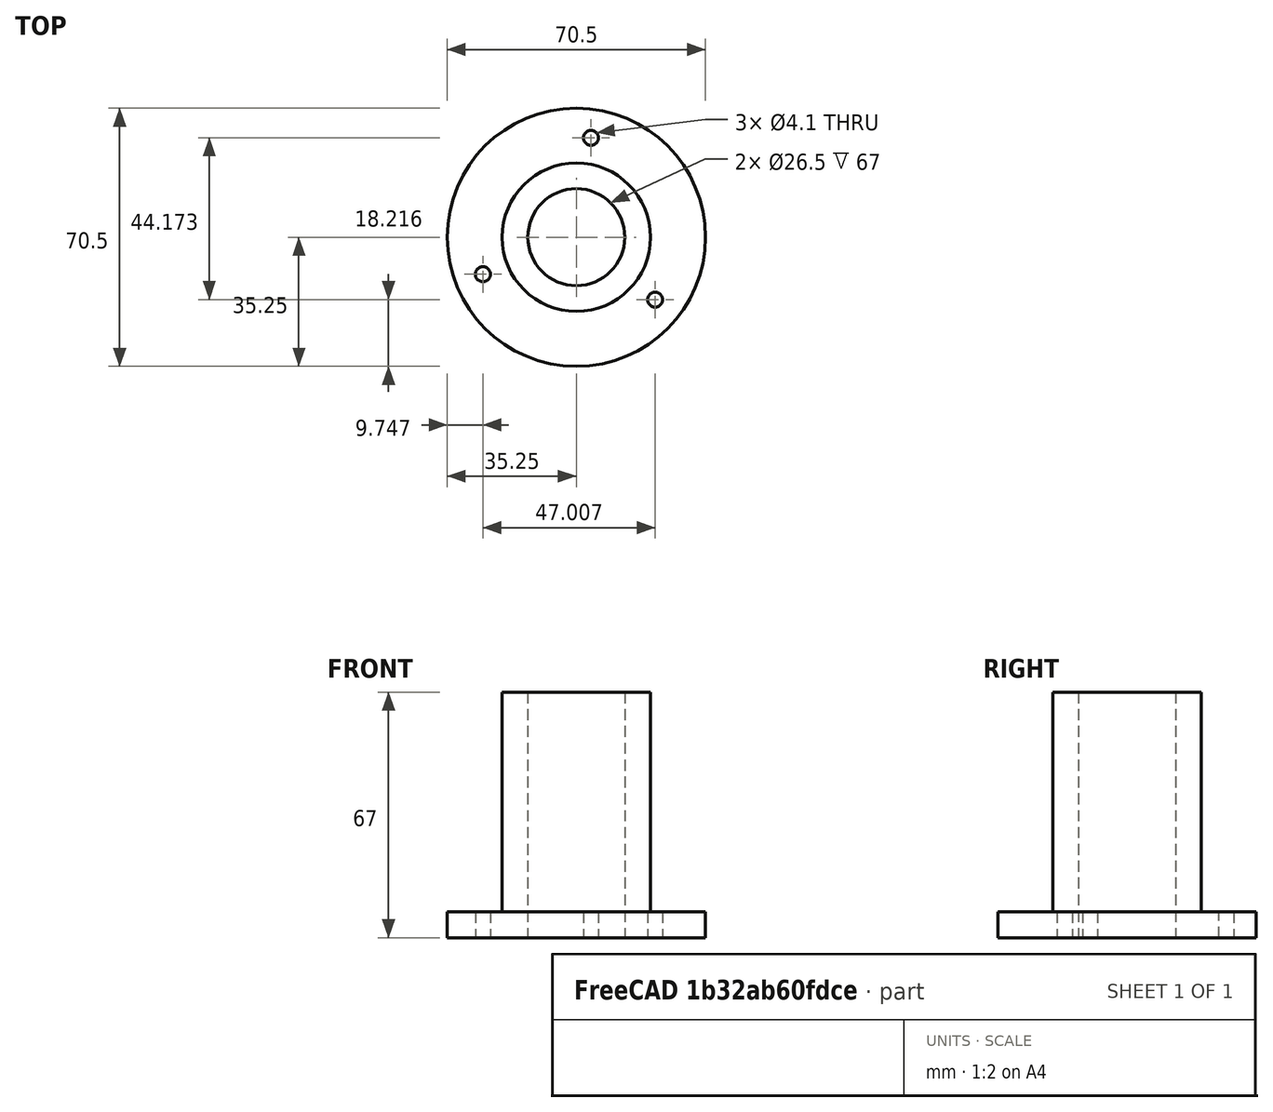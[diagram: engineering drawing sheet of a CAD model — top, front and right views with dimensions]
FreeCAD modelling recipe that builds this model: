
FCSTD DOCUMENT  (FreeCAD 1.1R38827 (Git))
Label: composit_stand3_sleeve_outer_model
License: All rights reserved
LicenseURL: http://en.wikipedia.org/wiki/All_rights_reserved
objects: PartDesign::SubShapeBinder×2, PartDesign::CoordinateSystem×2, PartDesign::Revolution×1, PartDesign::Body×1, Part::Feature×1
note: 9 computed .brp shape members not serialized (recipe doc carries the construction recipe); baked Part::Feature solids carry a one-line shape summary decoded from their .brp
EXTERNAL_REF file=composit_stand3_sleeve_outer_main.FCStd obj=Sketch

FEATURE [PartDesign::SubShapeBinder] Binder
  BindCopyOnChange = 0
  BindMode = 0
  ClaimChildren = true
  Fuse = false
  MakeFace = true
  OffsetFill = false
  OffsetIntersection = false
  OffsetJoinType = 0
  OffsetOpenResult = false
  PartialLoad = false
  Relative = false
  Support = -> [<external composit_stand3_sleeve_outer_main.FCStd>#Sketch]
  _Version = 2
FEATURE [PartDesign::SubShapeBinder] Binder001
  BindCopyOnChange = 0
  BindMode = 0
  ClaimChildren = true
  Context = -> Body [Binder001.]
  Fuse = false
  MakeFace = true
  OffsetFill = false
  OffsetIntersection = false
  OffsetJoinType = 0
  OffsetOpenResult = false
  PartialLoad = false
  Placement = pos=(0,0,0) rot=(1,0,0;1.5708rad)
  Relative = true
  Support = -> [Binder]
  _Version = 2
FEATURE [PartDesign::Revolution] Revolution
  Angle = 360
  Angle2 = 60
  Axis = (1e-16,1e-16,1)
  Base = (0,0,0)
  Placement = pos=(0,0,0) rot=(1,0,0;1.5708rad)
  Profile = -> Binder001 [Face1]
  ReferenceAxis = -> Z_Axis
  Reversed = true
  Suppressed = false
  Type = 0
FEATURE [PartDesign::CoordinateSystem] Local_CS  label="base_LCS"
  AttacherType = Attacher::AttachEngine3D
  AttachmentSupport = -> [XY_Plane]
  MapMode = 5
FEATURE [PartDesign::CoordinateSystem] Local_CS001
  AttacherType = Attacher::AttachEngine3D
  AttachmentOffset = pos=(0,0,67) rot=(1,0,0;3.14159rad)
  AttachmentSupport = -> [XY_Plane]
  MapMode = 5
  Placement = pos=(0,0,67) rot=(1,0,0;3.14159rad)
  expr: .AttachmentOffset.Base.z = <<composit_stand3_sleeve_outer_main>>#<<sleeve_outer_base_sketch>>.Constraints.height
FEATURE [PartDesign::Body] Body  label="sleeve_outer"
  AllowCompound = false
  Group = -> [Binder001,Revolution,Local_CS,Local_CS001]
  Origin = -> Origin
  Tip = -> Revolution
FEATURE [Part::Feature] Body170  label="sleeve_outer002"
  shape: bbox 70.5 x 70.5 x 67 mm, 9 faces (baked)
